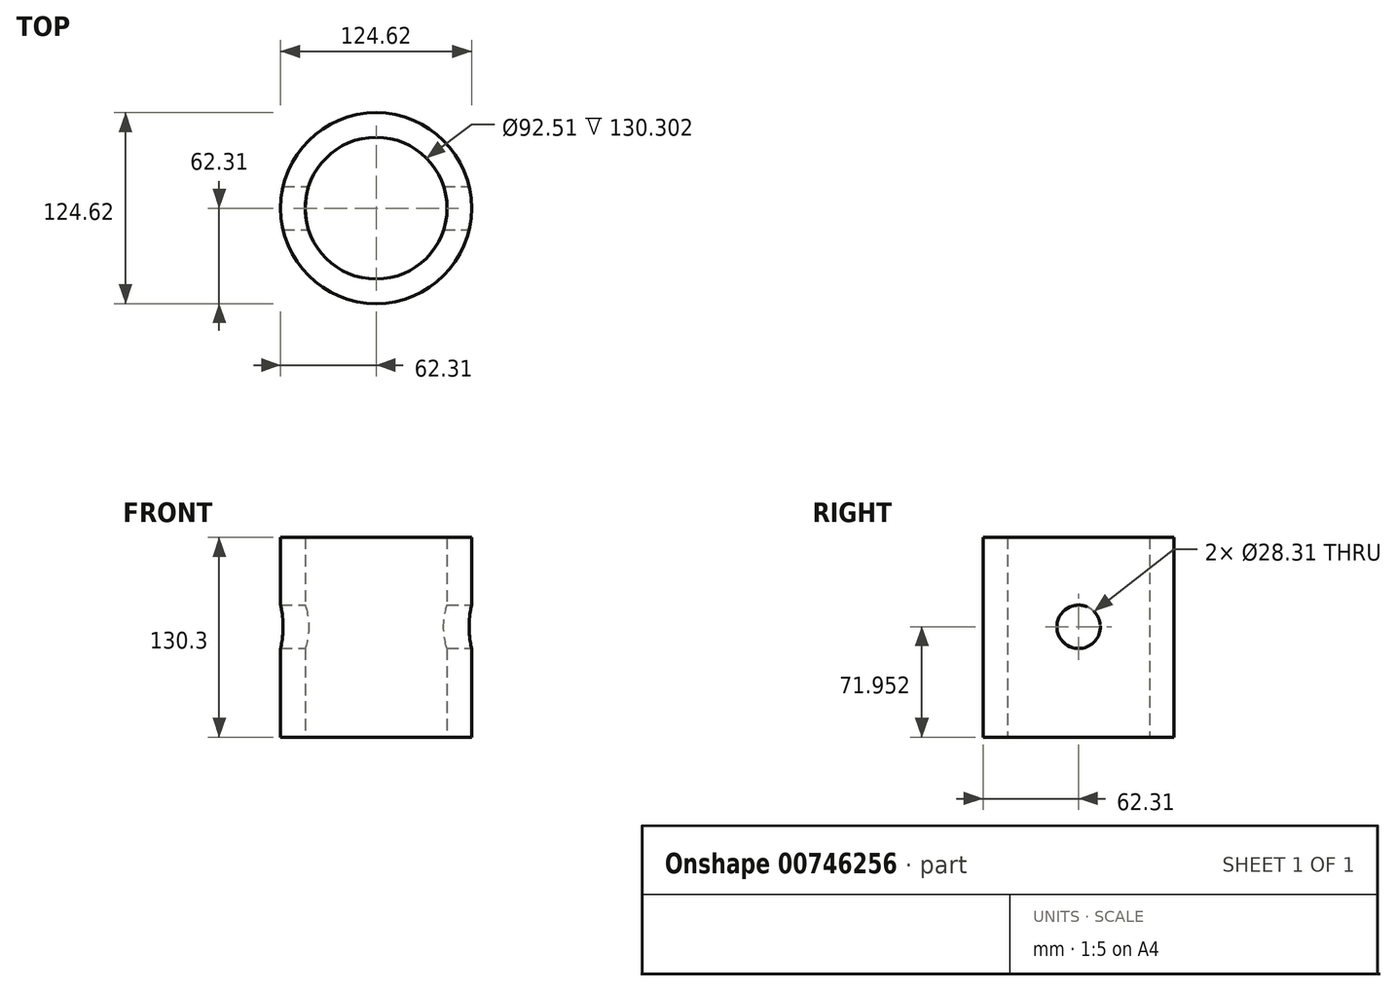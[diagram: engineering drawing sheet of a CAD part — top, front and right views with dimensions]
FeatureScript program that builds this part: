
annotation { "Feature Type Name" : "Feature", "Feature Type Description" : "" }
export const myFeature = defineFeature(function(context is Context, id is Id, definition is map)
    precondition{}
    {
        {
            var Q0;
            Q0=qCreatedBy(makeId("Top.planeOp"),FACE);
            var sketch = newSketch(context, id + "F0", { "sketchPlane" : qUnion([Q0])});
            skCircle(sketch, "E0", {"center": v(0, 0) * mm, "radius": 62.3 * mm});
            skCircle(sketch, "E1", {"center": v(0, 0) * mm, "radius": 46.26 * mm});
            skSolve(sketch);
        }
        {
            var Q0;
            Q0=makeQuery(id+"F0.imprint","IMPRINT",FACE,{"disambiguationData":[TD([[makeQuery(id+"F0.imprint","IMPRINT",EDGE,{"derivedFrom":sQuery(id+"F0.wireOp",EDGE,"E0")}),1.0]])]});
            extrude(context, id + "F1", {"entities" : qUnion([Q0]), "depth" : 130.3 * mm, "offsetDistance" : 25.4 * mm});
        }
        {
            var Q0;
            Q0=qCreatedBy(makeId("Right.planeOp"),FACE);
            var sketch = newSketch(context, id + "F2", { "sketchPlane" : qUnion([Q0])});
            skCircle(sketch, "E2", {"center": v(0, 71.95) * mm, "radius": 14.15 * mm});
            skSolve(sketch);
        }
        {
            var Q0;
            Q0=makeQuery(id+"F2.imprint","IMPRINT",FACE,{"disambiguationData":[TD([[makeQuery(id+"F2.imprint","IMPRINT",EDGE,{"derivedFrom":sQuery(id+"F2.wireOp",EDGE,"E2")}),1.0]])]});
            extrude(context, id + "F3", {"entities" : qUnion([Q0]), "operationType" : NewBodyOperationType.REMOVE, "endBound" : BoundingType.SYMMETRIC, "oppositeDirection" : true, "depth" : 127 * mm, "offsetDistance" : 25.4 * mm});
        }
    });
